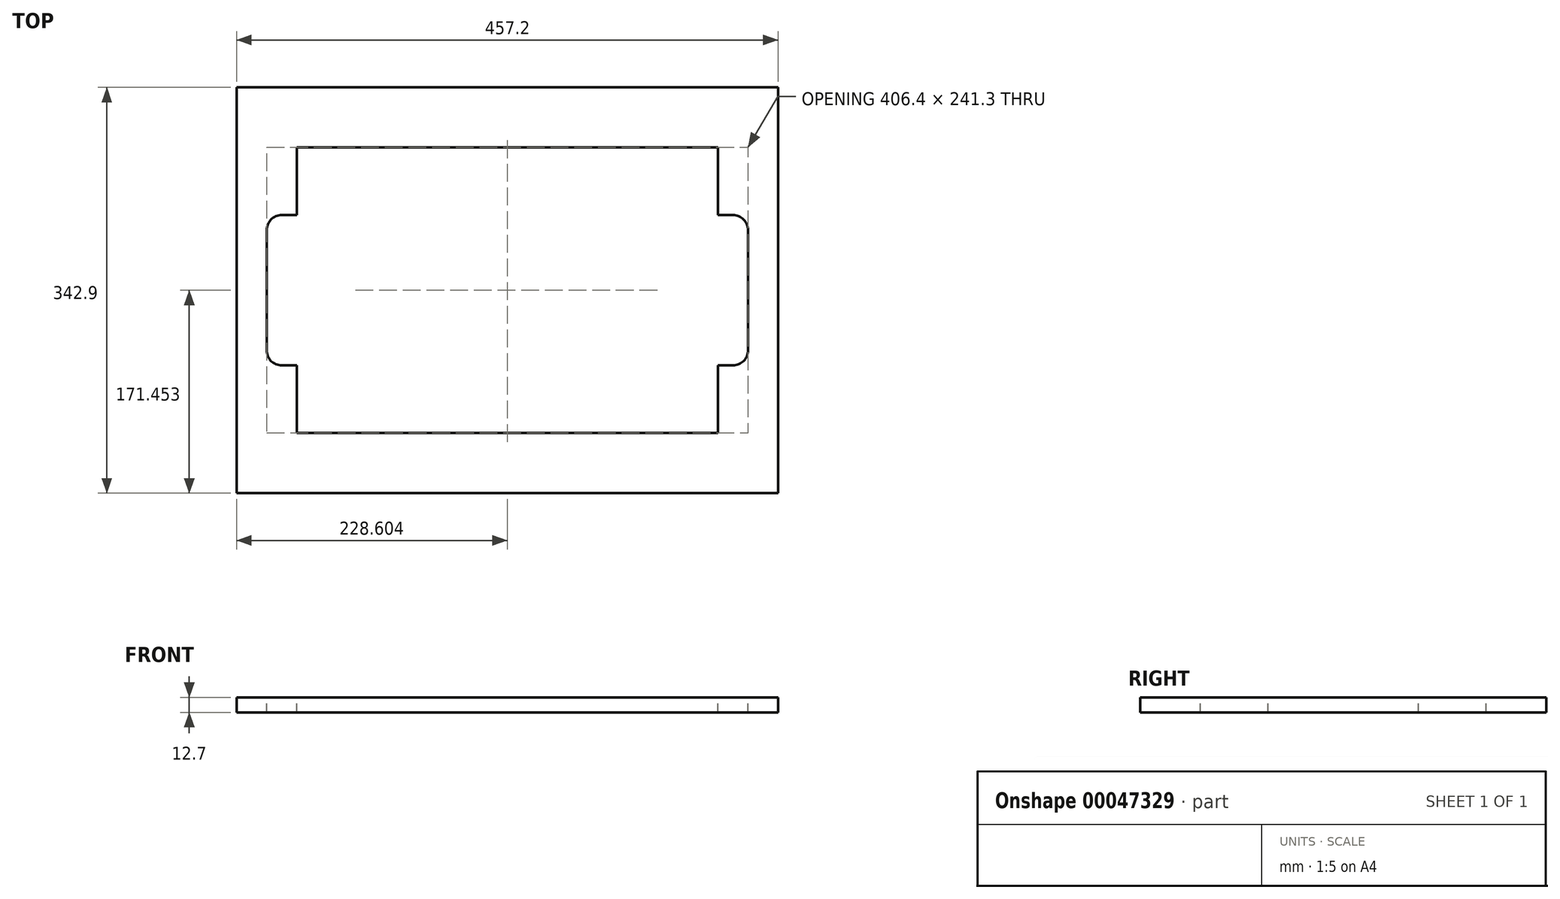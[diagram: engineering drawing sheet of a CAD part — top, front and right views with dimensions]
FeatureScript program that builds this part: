
annotation { "Feature Type Name" : "Feature", "Feature Type Description" : "" }
export const myFeature = defineFeature(function(context is Context, id is Id, definition is map)
    precondition{}
    {
        {
            var Q0;
            Q0=qCreatedBy(makeId("Top.planeOp"),FACE);
            var sketch = newSketch(context, id + "F0", { "sketchPlane" : qUnion([Q0])});
            skLineSegment(sketch, "E0.bottom", {"start": v(-43.92, 307.18) * mm, "end": v(413.28, 307.18) * mm});
            skLineSegment(sketch, "E0.top", {"start": v(-43.92, -35.72) * mm, "end": v(413.28, -35.72) * mm});
            skLineSegment(sketch, "E0.left", {"start": v(-43.92, 307.18) * mm, "end": v(-43.92, -35.72) * mm});
            skLineSegment(sketch, "E0.right", {"start": v(413.28, 307.18) * mm, "end": v(413.28, -35.72) * mm});
            skSolve(sketch);
        }
        {
            var Q0;
            Q0=makeQuery(id+"F0.imprint","IMPRINT",FACE,{"disambiguationData":[TD([[makeQuery(id+"F0.imprint","IMPRINT",EDGE,{"derivedFrom":sQuery(id+"F0.wireOp",EDGE,"E0.bottom")}),-1.0]])]});
            extrude(context, id + "F1", {"entities" : qUnion([Q0]), "depth" : 12.7 * mm});
        }
        {
            var Q0;
            Q0=makeQuery(id+"F1.opExtrude","CAP_FACE",FACE,{"disambiguationData":[OSD([sQuery(id+"F0.wireOp",EDGE,"E0.bottom"),sQuery(id+"F0.wireOp",EDGE,"E0.top"),sQuery(id+"F0.wireOp",EDGE,"E0.left"),sQuery(id+"F0.wireOp",EDGE,"E0.right")])],"isStart":false});
            var sketch = newSketch(context, id + "F2", { "sketchPlane" : qUnion([Q0])});
            skLineSegment(sketch, "E1.bottom", {"start": v(6.88, 256.38) * mm, "end": v(362.48, 256.38) * mm});
            skLineSegment(sketch, "E1.top", {"start": v(6.88, 15.08) * mm, "end": v(362.48, 15.08) * mm});
            skLineSegment(sketch, "E1.left", {"start": v(6.88, 256.38) * mm, "end": v(6.88, 15.08) * mm});
            skLineSegment(sketch, "E1.right", {"start": v(362.48, 256.38) * mm, "end": v(362.48, 15.08) * mm});
            skSolve(sketch);
        }
        {
            var Q0;
            Q0=makeQuery(id+"F2.imprint","IMPRINT",FACE,{"disambiguationData":[TD([[makeQuery(id+"F2.imprint","IMPRINT",EDGE,{"derivedFrom":sQuery(id+"F2.wireOp",EDGE,"E1.bottom")}),-1.0]])]});
            extrude(context, id + "F3", {"entities" : qUnion([Q0]), "operationType" : NewBodyOperationType.REMOVE, "oppositeDirection" : true, "depth" : 25.4 * mm});
        }
        {
            var Q0;
            Q0=makeQuery(id+"F1.opExtrude","CAP_FACE",FACE,{"disambiguationData":[OSD([sQuery(id+"F0.wireOp",EDGE,"E0.bottom"),sQuery(id+"F0.wireOp",EDGE,"E0.top"),sQuery(id+"F0.wireOp",EDGE,"E0.left"),sQuery(id+"F0.wireOp",EDGE,"E0.right")])],"isStart":false});
            var sketch = newSketch(context, id + "F4", { "sketchPlane" : qUnion([Q0])});
            skLineSegment(sketch, "E2.bottom", {"start": v(6.88, 199.23) * mm, "end": v(-18.52, 199.23) * mm});
            skLineSegment(sketch, "E2.top", {"start": v(6.88, 72.23) * mm, "end": v(-18.52, 72.23) * mm});
            skLineSegment(sketch, "E2.left", {"start": v(6.88, 199.23) * mm, "end": v(6.88, 72.23) * mm});
            skLineSegment(sketch, "E2.right", {"start": v(-18.52, 199.23) * mm, "end": v(-18.52, 72.23) * mm});
            skLineSegment(sketch, "E3.bottom", {"start": v(362.48, 199.23) * mm, "end": v(387.88, 199.23) * mm});
            skLineSegment(sketch, "E3.top", {"start": v(362.48, 72.23) * mm, "end": v(387.88, 72.23) * mm});
            skLineSegment(sketch, "E3.left", {"start": v(362.48, 199.23) * mm, "end": v(362.48, 72.23) * mm});
            skLineSegment(sketch, "E3.right", {"start": v(387.88, 199.23) * mm, "end": v(387.88, 72.23) * mm});
            skSolve(sketch);
        }
        {
            var Q0;
            Q0=makeQuery(id+"F4.imprint","IMPRINT",FACE,{"disambiguationData":[TD([[makeQuery(id+"F4.imprint","IMPRINT",EDGE,{"derivedFrom":sQuery(id+"F4.wireOp",EDGE,"E2.bottom")}),1.0]])]});
            var Q1;
            Q1=makeQuery(id+"F4.imprint","IMPRINT",FACE,{"disambiguationData":[TD([[makeQuery(id+"F4.imprint","IMPRINT",EDGE,{"derivedFrom":sQuery(id+"F4.wireOp",EDGE,"E3.bottom")}),-1.0]])]});
            extrude(context, id + "F5", {"entities" : qUnion([Q0, Q1]), "operationType" : NewBodyOperationType.REMOVE, "oppositeDirection" : true, "depth" : 25.4 * mm});
        }
        {
            var Q0;
            Q0=makeQuery(id+"F5.boolean.opBoolean","COPY",EDGE,{"derivedFrom":makeQuery(id+"F5.opExtrude","SWEPT_EDGE",EDGE,{"disambiguationData":[OSD([sQuery(id+"F4.wireOp",EDGE,"E2.bottom"),sQuery(id+"F4.wireOp",EDGE,"E2.right")])]})});
            var Q1;
            Q1=makeQuery(id+"F5.boolean.opBoolean","COPY",EDGE,{"derivedFrom":makeQuery(id+"F5.opExtrude","SWEPT_EDGE",EDGE,{"disambiguationData":[OSD([sQuery(id+"F4.wireOp",EDGE,"E3.bottom"),sQuery(id+"F4.wireOp",EDGE,"E3.right")])]})});
            var Q2;
            Q2=makeQuery(id+"F5.boolean.opBoolean","COPY",EDGE,{"derivedFrom":makeQuery(id+"F5.opExtrude","SWEPT_EDGE",EDGE,{"disambiguationData":[OSD([sQuery(id+"F4.wireOp",EDGE,"E2.top"),sQuery(id+"F4.wireOp",EDGE,"E2.right")])]})});
            var Q3;
            Q3=makeQuery(id+"F5.boolean.opBoolean","COPY",EDGE,{"derivedFrom":makeQuery(id+"F5.opExtrude","SWEPT_EDGE",EDGE,{"disambiguationData":[OSD([sQuery(id+"F4.wireOp",EDGE,"E3.top"),sQuery(id+"F4.wireOp",EDGE,"E3.right")])]})});
            fillet(context, id + "F6", {"entities" : qUnion([Q0, Q1, Q2, Q3]), "radius" : 12.7 * mm, "tangentPropagation" : true, "allowEdgeOverflow" : false});
        }
    });
